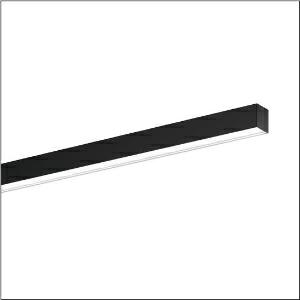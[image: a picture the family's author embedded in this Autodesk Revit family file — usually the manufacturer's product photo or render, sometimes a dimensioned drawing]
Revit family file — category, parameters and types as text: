
# Revit family: silica_r__21_51mx23tctab_c65d
name_source: partatom
category: Lighting Fixtures
units: mm (PartAtom-declared; Revit-internal decimal feet)

## family parameters
Cut with Voids When Loaded = No
Host = Face
Light Source = No
Part Type = Normal
Room Calculation Point = No
Round Connector Dimension = Use Diameter
Shared = No

## types (1)
- --- (1 x LED, 8070 lm, 81.1 W, 6500K)
    Apparent Load = 81 VA
    CIE Flux Codes = 78 96 99 100 100
    Color Rendering = 80
    Color Temperature = 6500K
    Default Elevation = 1800 mm
    Description = Silica® 21, office luminaire, primary optical cover: prismatic diffuser, of PMMA, CAT 2 (L<= 3000cd/m²), light emission: direct distribution, primary light characteristic: symmetric, installation type: surface-mounted, LED, rated luminous flux: 8.070lm, luminous efficacy: 95lm/W, light colour: 8tw, colour temperature: 2700..6500K, control gear: ECG DALI, with terminal, 3+2-pole, max. 2.5mm², mains connection: 220..240V, AC, 50/60Hz, rated input power: 85.1W, luminaire housing, of aluminium, jet black (RAL 9005), length: 3.004mm, width: 53mm, height: 53mm, protection rating (complete): IP20, insulation class (complete): insulation class I (protective earthing), certification: CE, permissible operating ambient temperature: 0..+35°C, standard: EN 50419, packaging unit: 1 piece
    Height = 0 mm  [stored 0 ft]
    Lamp = 1 x LED
    Lamp Light Flux = 8070 lm
    Lamp Power = 81.1 W
    Lamp count = 1
    Length = 3004 mm
    Luminous efficacy = 100 lm/W
    Manufacturer = Siteco
    ModVariant = No
    Model = 51MX23TCTAB
    Mounting Place = Ceiling
    Mounting Type = Recessed
    Number of Poles = 1
    OnlyDefault = Yes
    Power Factor = 1
    Product Name = Silica® 21
    Product group = office luminaire | ceiling recessed
    ProductGroupID = 400
    Protection Class = Protection class I
    Protection Degree = IP 20
    RLX_Detail_Level = 1
    RLX_Emergency_Light_Flux = 0 lm
    RLX_Emergency_Type = 0
    RLX_Emergency_Type_DB = No
    RlxData = <blob elided: 20381 chars, md5=15cf263b>
    Socket = socket
    Standby Power = 0 W
    System Light Flux = 8070 lm
    System Power = 81 W
    Type Comments = individual setting
    Type Image = l_1335925.jpg
    URL = http://relux.com
    VarID = @adj_109609
    Voltage = 0 V
    Weight = 0.00 kg
    Width = 53 mm

note: [stored X ft] marks values corroborated as IEEE doubles in the binary element streams (Revit-internal decimal feet)

## geometry (parser evidence)
native form markers: Blend x4, Sweep x10
no freeform markers — native parametric forms only
